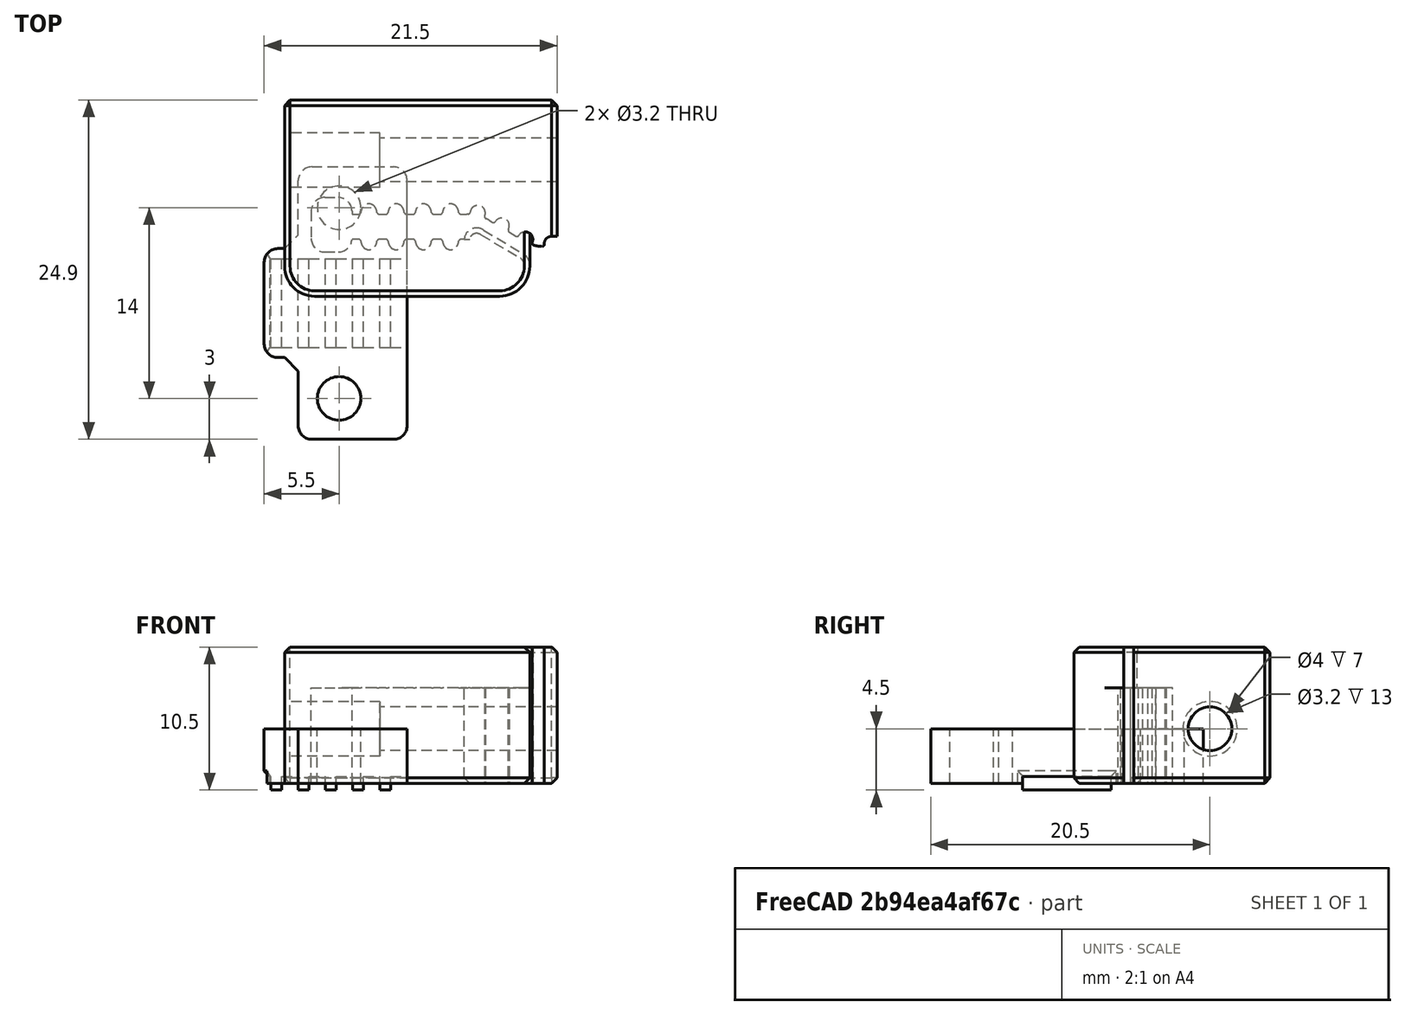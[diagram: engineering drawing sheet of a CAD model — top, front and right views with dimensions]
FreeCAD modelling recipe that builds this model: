
FCSTD DOCUMENT  (FreeCAD 0.19R24291 (Git))
Label: belt-clamp-tesioner
License: All rights reserved
LicenseURL: http://en.wikipedia.org/wiki/All_rights_reserved
objects: Part::Box×15, Part::MultiFuse×8, Part::Cut×6, Part::Cylinder×4, Part::Fillet×3, Part::Chamfer×3, Part::Feature×2, Part::Refine×1
note: 42 computed .brp shape members not serialized (recipe doc carries the construction recipe); baked Part::Feature solids carry a one-line shape summary decoded from their .brp

FEATURE [Part::Cylinder] Cylinder011
  Angle = 360
  AttacherType = Attacher::AttachEngine3D
  Height = 10
  Placement = pos=(0,7,0) rot=(0,0,1;0rad)
  Radius = 1.6
FEATURE [Part::Cylinder] Cylinder012
  Angle = 360
  AttacherType = Attacher::AttachEngine3D
  Height = 10
  Placement = pos=(0,-7,0) rot=(0,0,1;0rad)
  Radius = 1.6
FEATURE [Part::Box] Box008  label="Cube008"
  AttacherType = Attacher::AttachEngine3D
  Height = 4
  Length = 8
  Placement = pos=(-3,-10,0) rot=(0,0,1;0rad)
  Width = 20
FEATURE [Part::MultiFuse] Fusion017
  Shapes = -> [Cylinder011,Cylinder012]
FEATURE [Part::Fillet] Fillet002
  Base = -> Box008
  Edges = 4 edges r=1: [Edge1,Edge3,Edge5,Edge7]
FEATURE [Part::Cut] Cut008004003012001003001009
  Base = -> Fillet002
  Tool = -> Fusion017
FEATURE [Part::Box] Box036  label="Cube032"
  AttacherType = Attacher::AttachEngine3D
  Height = 10
  Length = 20
  Placement = pos=(-4,0.5,0) rot=(0,0,1;0rad)
  Width = 14.4
FEATURE [Part::Cylinder] Cylinder033
  Angle = 360
  AttacherType = Attacher::AttachEngine3D
  Height = 7
  Placement = pos=(3,10.5,4) rot=(0.57735,-0.57735,-0.57735;2.0944rad)
  Radius = 2
FEATURE [Part::Feature] Cut008004004001  label="Cut008004005"
  shape: bbox 30 x 15.4 x 10 mm, 103 faces (baked)
FEATURE [Part::Cylinder] Cylinder034
  Angle = 360
  AttacherType = Attacher::AttachEngine3D
  Height = 24
  Placement = pos=(18,10.5,4) rot=(0.57735,-0.57735,-0.57735;2.0944rad)
  Radius = 1.6
FEATURE [Part::MultiFuse] Fusion001007002
  Shapes = -> [Cylinder034,Cylinder033]
FEATURE [Part::Box] Box037  label="Cube033"
  AttacherType = Attacher::AttachEngine3D
  Height = 10
  Length = 10
  Placement = pos=(14,-3,0) rot=(0,0,1;0rad)
  Width = 10
FEATURE [Part::Cut] Cut008004004002
  Base = -> Box037
  Placement = pos=(0,0,6) rot=(0,0,1;0rad)
  Tool = -> Cut008004004001
FEATURE [Part::Feature] Extrude001001  label="belt-cut001"
  Placement = pos=(-0.3,-1.1,-3) rot=(0,0,1;0rad)
  shape: bbox 18.15 x 13.85 x 7 mm, 84 faces (baked)
FEATURE [Part::Cut] Cut008004004003
  Base = -> Box036
  Tool = -> Extrude001001
FEATURE [Part::Cut] Cut008004004004
  Base = -> Cut008004004003
  Tool = -> Cut008004004002
FEATURE [Part::Cut] Cut008004004005
  Base = -> Cut008004004004
  Tool = -> Fusion001007002
FEATURE [Part::Refine] Cut008004004005001
  Source = -> Cut008004004005
FEATURE [Part::Fillet] Fillet010
  Base = -> Cut008004004005001
  Edges = 2 edges r=2.2: [Edge1,Edge7]
FEATURE [Part::Chamfer] Chamfer008009  label="belt-tesioner-block"
  Base = -> Fillet010
  Edges = 17 edges r=0.4: [Edge1,Edge3,Edge4,Edge6,Edge13,Edge14,Edge15,Edge16,Edge17,Edge18,Edge20,Edge21,Edge23,Edge24,Edge102,Edge103,Edge104]
FEATURE [Part::Box] Box038  label="Cube034"
  AttacherType = Attacher::AttachEngine3D
  Height = 0.5
  Length = 0.8
  Placement = pos=(-1.8,-3.25,-0.5) rot=(0,0,1;0rad)
  Width = 6.5
FEATURE [Part::Box] Box039  label="Cube035"
  AttacherType = Attacher::AttachEngine3D
  Height = 0.5
  Length = 1.2
  Placement = pos=(-3,-3.25,0) rot=(0,0,1;0rad)
  Width = 6.5
FEATURE [Part::Box] Box040  label="Cube036"
  AttacherType = Attacher::AttachEngine3D
  Height = 0.5
  Length = 0.8
  Placement = pos=(0.2,-3.25,-0.5) rot=(0,0,1;0rad)
  Width = 6.5
FEATURE [Part::Box] Box041  label="Cube037"
  AttacherType = Attacher::AttachEngine3D
  Height = 0.5
  Length = 0.8
  Placement = pos=(2.2,-3.25,-0.5) rot=(0,0,1;0rad)
  Width = 6.5
FEATURE [Part::Box] Box042  label="Cube038"
  AttacherType = Attacher::AttachEngine3D
  Height = 0.5
  Length = 0.8
  Placement = pos=(4.2,-3.25,-0.5) rot=(0,0,1;0rad)
  Width = 6.5
FEATURE [Part::Box] Box043  label="Cube039"
  AttacherType = Attacher::AttachEngine3D
  Height = 0.5
  Length = 1.2
  Placement = pos=(-1,-3.25,0) rot=(0,0,1;0rad)
  Width = 6.5
FEATURE [Part::Box] Box044  label="Cube040"
  AttacherType = Attacher::AttachEngine3D
  Height = 0.5
  Length = 1.2
  Placement = pos=(1,-3.25,0) rot=(0,0,1;0rad)
  Width = 6.5
FEATURE [Part::Box] Box045  label="Cube041"
  AttacherType = Attacher::AttachEngine3D
  Height = 0.5
  Length = 1.2
  Placement = pos=(3,-3.25,0) rot=(0,0,1;0rad)
  Width = 6.5
FEATURE [Part::MultiFuse] Fusion001007011047
  Placement = pos=(0.8,0,0) rot=(0,0,1;0rad)
  Shapes = -> [Box045,Box044,Box043,Box039]
FEATURE [Part::MultiFuse] Fusion001007011046
  Placement = pos=(-1.2,0,0) rot=(0,0,1;0rad)
  Shapes = -> [Box042,Box041,Box040,Box038]
FEATURE [Part::Box] Box046  label="Cube042"
  AttacherType = Attacher::AttachEngine3D
  Height = 4
  Length = 3
  Placement = pos=(-5.5,-4,0) rot=(0,0,1;0rad)
  Width = 8
FEATURE [Part::MultiFuse] Fusion001007011048
  Shapes = -> [Cut008004003012001003001009,Box046]
FEATURE [Part::Fillet] Fillet
  Base = -> Fusion001007011048
  Edges = 2 edges r=1: [Edge1,Edge3]
FEATURE [Part::Chamfer] Chamfer008010
  Base = -> Fillet
  Edges = 2 edges r=1: [Edge17,Edge21]
FEATURE [Part::Box] Box047  label="Cube043"
  AttacherType = Attacher::AttachEngine3D
  Height = 0.5
  Length = 0.8
  Placement = pos=(-5,-3.25,-0.5) rot=(0,0,1;0rad)
  Width = 6.5
FEATURE [Part::Box] Box048  label="Cube044"
  AttacherType = Attacher::AttachEngine3D
  Height = 0.5
  Length = 1.2
  Placement = pos=(-4.2,-3.25,0) rot=(0,0,1;0rad)
  Width = 6.5
FEATURE [Part::MultiFuse] Fusion001007011049
  Shapes = -> [Box047,Fusion001007011046]
FEATURE [Part::MultiFuse] Fusion001007011051
  Shapes = -> [Chamfer008010,Fusion001007011049]
FEATURE [Part::Box] Box049  label="Cube045"
  AttacherType = Attacher::AttachEngine3D
  Height = 0.5
  Length = 1.2
  Placement = pos=(-6.2,-3.25,0) rot=(0,0,1;0rad)
  Width = 6.5
FEATURE [Part::MultiFuse] Fusion001007011052
  Shapes = -> [Fusion001007011047,Box048,Box049]
FEATURE [Part::Cut] Cut008004003012001003001010001023
  Base = -> Fusion001007011051
  Tool = -> Fusion001007011052
FEATURE [Part::Chamfer] Chamfer008011  label="belt-clamp"
  Base = -> Cut008004003012001003001010001023
  Edges = 5 edges r=0.4: [Edge12,Edge13,Edge16,Edge18,Edge19]
